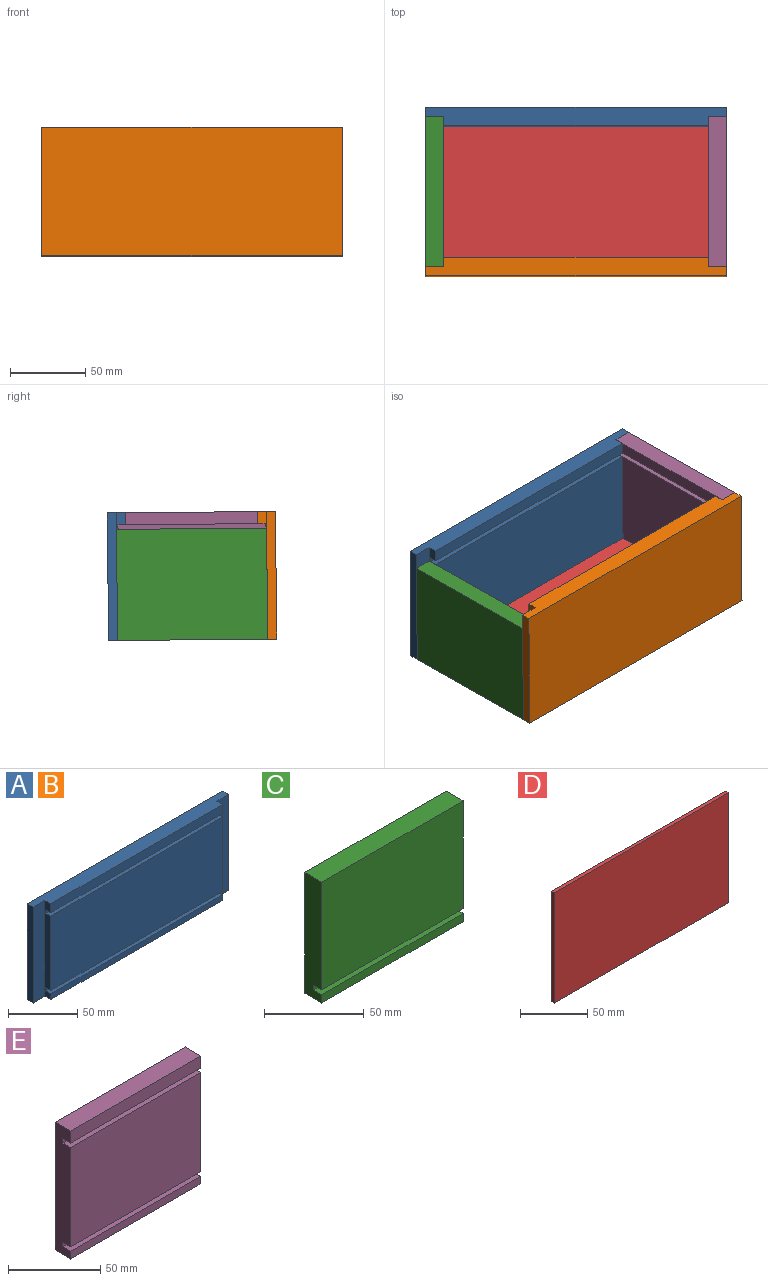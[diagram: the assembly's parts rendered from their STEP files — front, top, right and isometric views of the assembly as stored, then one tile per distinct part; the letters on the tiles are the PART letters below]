
ASSEMBLY  parts=5 mates=4
PART A: 18 faces, bbox 200x12x85 mm
  f0: plane 176x8mm, normal (0,-1,0), area 1408mm2, adj f2,f4,f11,f16
  f1: plane 176x66mm, normal (0,-1,0), area 11616mm2, adj f2,f11,f13,f15
  f2: plane 85x6mm, normal (1,0,0), area 480mm2, adj f0,f1,f4,f6,f7,f9,f12,f13
  f3: plane 85x6mm, normal (1,0,0), area 510mm2, adj f4,f7,f8,f9
  f4: plane 200x12mm, normal (0,0,1), area 2256mm2, adj f0,f2,f3,f5,f8,f9,f10,f11
  f5: plane 85x6mm, normal (-1,0,0), area 510mm2, adj f4,f7,f8,f10
  f6: plane 176x5mm, normal (0,-1,0), area 880mm2, adj f2,f7,f11,f12
  f7: plane 200x12mm, normal (0,0,-1), area 2256mm2, adj f2,f3,f5,f6,f8,f9,f10,f11
  f8: plane 200x85mm, normal (0,1,0), area 17000mm2, adj f3,f4,f5,f7
  f9: plane 85x12mm, normal (0,-1,0), area 1020mm2, adj f2,f3,f4,f7
  f10: plane 85x12mm, normal (0,-1,0), area 1020mm2, adj f4,f5,f7,f11
  f11: plane 85x6mm, normal (-1,0,0), area 480mm2, adj f0,f1,f4,f6,f7,f10,f12,f13
  f12: plane 176x5mm, normal (0,0,1), area 880mm2, adj f2,f6,f11,f14
  f13: plane 176x5mm, normal (0,0,-1), area 880mm2, adj f1,f2,f11,f14
  f14: plane 176x3mm, normal (0,-1,0), area 528mm2, adj f2,f11,f12,f13
  f15: plane 176x5mm, normal (0,0,1), area 880mm2, adj f1,f2,f11,f17
  f16: plane 176x5mm, normal (0,0,-1), area 880mm2, adj f0,f2,f11,f17
  f17: plane 176x3mm, normal (0,-1,0), area 528mm2, adj f2,f11,f15,f16
PART B: same geometry as A
PART C: 10 faces, bbox 100x12x74 mm
  f0: plane 100x5mm, normal (0,-1,0), area 500mm2, adj f1,f2,f3,f8
  f1: plane 74x12mm, normal (-1,0,0), area 870mm2, adj f0,f2,f4,f5,f6,f7,f8,f9
  f2: plane 100x12mm, normal (0,0,-1), area 1200mm2, adj f0,f1,f3,f6
  f3: plane 74x12mm, normal (1,0,0), area 870mm2, adj f0,f2,f4,f5,f6,f7,f8,f9
  f4: plane 100x12mm, normal (0,0,1), area 1200mm2, adj f1,f3,f5,f6
  f5: plane 100x66mm, normal (0,-1,0), area 6600mm2, adj f1,f3,f4,f7
  f6: plane 100x74mm, normal (0,1,0), area 7400mm2, adj f1,f2,f3,f4
  f7: plane 100x6mm, normal (0,0,-1), area 600mm2, adj f1,f3,f5,f9
  f8: plane 100x6mm, normal (0,0,1), area 600mm2, adj f0,f1,f3,f9
  f9: plane 100x3mm, normal (0,-1,0), area 300mm2, adj f1,f3,f7,f8
PART D: 6 faces, bbox 182x3x100 mm
  f0: plane 182x3mm, normal (0,0,-1), area 546mm2, adj f1,f3,f4,f5
  f1: plane 100x3mm, normal (1,0,0), area 300mm2, adj f0,f2,f4,f5
  f2: plane 182x3mm, normal (0,0,1), area 546mm2, adj f1,f3,f4,f5
  f3: plane 100x3mm, normal (-1,0,0), area 300mm2, adj f0,f2,f4,f5
  f4: plane 182x100mm, normal (0,-1,0), area 18200mm2, adj f0,f1,f2,f3
  f5: plane 182x100mm, normal (0,1,0), area 18200mm2, adj f0,f1,f2,f3
PART E: 14 faces, bbox 100x12x85 mm
  f0: plane 100x66mm, normal (0,-1,0), area 6600mm2, adj f2,f4,f9,f12
  f1: plane 100x8mm, normal (0,-1,0), area 800mm2, adj f2,f4,f5,f11
  f2: plane 85x12mm, normal (-1,0,0), area 984mm2, adj f0,f1,f3,f5,f6,f7,f8,f9
  f3: plane 100x12mm, normal (0,0,-1), area 1200mm2, adj f2,f4,f6,f7
  f4: plane 85x12mm, normal (1,0,0), area 984mm2, adj f0,f1,f3,f5,f6,f7,f8,f9
  f5: plane 100x12mm, normal (0,0,1), area 1200mm2, adj f1,f2,f4,f7
  f6: plane 100x5mm, normal (0,-1,0), area 500mm2, adj f2,f3,f4,f8
  f7: plane 100x85mm, normal (0,1,0), area 8500mm2, adj f2,f3,f4,f5
  f8: plane 100x6mm, normal (0,0,1), area 600mm2, adj f2,f4,f6,f10
  f9: plane 100x6mm, normal (0,0,-1), area 600mm2, adj f0,f2,f4,f10
  f10: plane 100x3mm, normal (0,-1,0), area 300mm2, adj f2,f4,f8,f9
  f11: plane 100x6mm, normal (0,0,-1), area 600mm2, adj f1,f2,f4,f13
  f12: plane 100x6mm, normal (0,0,1), area 600mm2, adj f0,f2,f4,f13
  f13: plane 100x3mm, normal (0,-1,0), area 300mm2, adj f2,f4,f11,f12
PLACE A rot(axis=(-1,0,0),0.5deg) t=(116.27,-151.88,48.76)mm
PLACE B rot(axis=(0,0,-1),180deg) t=(116.27,-263.88,49.78)mm
PLACE C rot(axis=(0,0,1),90deg) t=(16.27,-207.93,43.77)mm
PLACE D rot(axis=(1,0,0),89.5deg) t=(116.27,-209.2,14.78)mm
PLACE E rot(axis=(0,0,-1),90deg) t=(216.27,-207.88,49.27)mm
MATE fastened E.f2 <-> A.f9  axis (0,1,-0.01) through (216.27,-157.88,48.81)mm
MATE fastened B.f10 <-> E.f4  axis (0,1,-0.01) through (216.27,-257.88,49.73)mm
MATE fastened A.f14 <-> D.f0  axis (0,-1,0.01) through (116.27,-159.21,12.82)mm
MATE fastened A.f10 <-> C.f3  axis (0,-1,0.01) through (22.27,-158.27,6.31)mm
